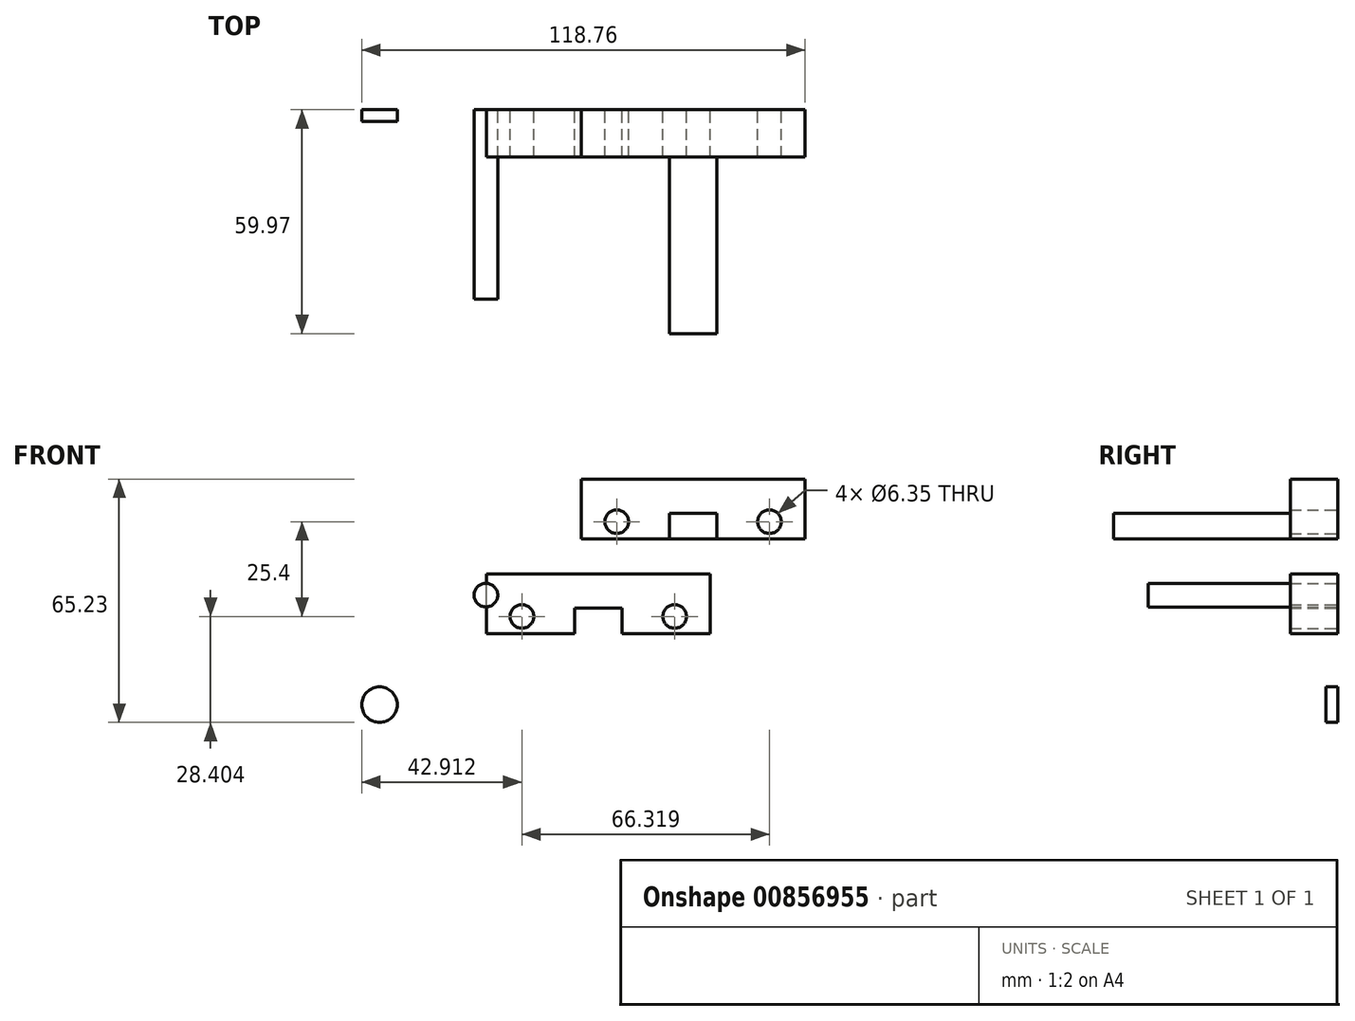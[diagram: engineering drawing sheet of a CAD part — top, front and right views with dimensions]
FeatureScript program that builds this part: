
annotation { "Feature Type Name" : "Feature", "Feature Type Description" : "" }
export const myFeature = defineFeature(function(context is Context, id is Id, definition is map)
    precondition{}
    {
        {
            var Q0;
            Q0=qCreatedBy(makeId("Front.planeOp"),FACE);
            var sketch = newSketch(context, id + "F0", { "sketchPlane" : qUnion([Q0])});
            skLineSegment(sketch, "E0", {"start": v(-17.85, 21.68) * mm, "end": v(42.12, 21.68) * mm});
            skLineSegment(sketch, "E1", {"start": v(42.12, 21.68) * mm, "end": v(42.12, 5.66) * mm});
            skLineSegment(sketch, "E2", {"start": v(-17.85, 5.66) * mm, "end": v(-17.85, 21.68) * mm});
            skLineSegment(sketch, "E3", {"start": v(-17.85, 5.66) * mm, "end": v(5.78, 5.66) * mm});
            skLineSegment(sketch, "E4", {"start": v(5.78, 5.66) * mm, "end": v(5.78, 12.52) * mm});
            skLineSegment(sketch, "E5", {"start": v(5.78, 12.52) * mm, "end": v(18.48, 12.52) * mm});
            skLineSegment(sketch, "E6", {"start": v(18.48, 12.52) * mm, "end": v(18.48, 5.66) * mm});
            skLineSegment(sketch, "E7", {"start": v(18.48, 5.66) * mm, "end": v(42.12, 5.66) * mm});
            skCircle(sketch, "E8", {"center": v(32.6, 10.25) * mm, "radius": 3.18 * mm});
            skCircle(sketch, "E9", {"center": v(-8.33, 10.25) * mm, "radius": 3.18 * mm});
            skSolve(sketch);
        }
        {
            var Q0;
            Q0=makeQuery(id+"F0.imprint","IMPRINT",FACE,{"disambiguationData":[TD([[makeQuery(id+"F0.imprint","IMPRINT",EDGE,{"derivedFrom":sQuery(id+"F0.wireOp",EDGE,"E0")}),-1.0]])]});
            extrude(context, id + "F1", {"entities" : qUnion([Q0]), "surfaceOperationType" : NewSurfaceOperationType.ADD, "depth" : 12.7 * mm, "offsetDistance" : 25.4 * mm});
        }
        {
            var Q0;
            Q0=makeQuery(id+"F1.opExtrude","SWEPT_BODY",BODY,{"disambiguationData":[OSD([sQuery(id+"F0.wireOp",EDGE,"E0"),sQuery(id+"F0.wireOp",EDGE,"E1"),sQuery(id+"F0.wireOp",EDGE,"E2"),sQuery(id+"F0.wireOp",EDGE,"E3"),sQuery(id+"F0.wireOp",EDGE,"E4"),sQuery(id+"F0.wireOp",EDGE,"E5"),sQuery(id+"F0.wireOp",EDGE,"E6"),sQuery(id+"F0.wireOp",EDGE,"E7")])]});
            transform(context, id + "F2", {"entities" : qUnion([Q0]), "transformType" : TransformType.TRANSLATION_3D, "dx" : 25.4 * mm, "dy" : 0 * mm, "dz" : 25.4 * mm, "makeCopy" : true});
        }
        {
            var Q0;
            Q0=makeQuery(id+"F2.opPattern","COPY",FACE,{"derivedFrom":makeQuery(id+"F1.opExtrude","CAP_FACE",FACE,{"disambiguationData":[OSD([sQuery(id+"F0.wireOp",EDGE,"E0"),sQuery(id+"F0.wireOp",EDGE,"E1"),sQuery(id+"F0.wireOp",EDGE,"E2"),sQuery(id+"F0.wireOp",EDGE,"E3"),sQuery(id+"F0.wireOp",EDGE,"E4"),sQuery(id+"F0.wireOp",EDGE,"E5"),sQuery(id+"F0.wireOp",EDGE,"E6"),sQuery(id+"F0.wireOp",EDGE,"E7")])],"isStart":true}),"instanceName":"1"});
            var sketch = newSketch(context, id + "F3", { "sketchPlane" : qUnion([Q0])});
            skLineSegment(sketch, "E10.bottom", {"start": v(-43.88, 31.06) * mm, "end": v(-31.18, 31.06) * mm});
            skLineSegment(sketch, "E10.top", {"start": v(-43.88, 37.92) * mm, "end": v(-31.18, 37.92) * mm});
            skLineSegment(sketch, "E10.left", {"start": v(-43.88, 31.06) * mm, "end": v(-43.88, 37.92) * mm});
            skLineSegment(sketch, "E10.right", {"start": v(-31.18, 31.06) * mm, "end": v(-31.18, 37.92) * mm});
            skCircle(sketch, "E11", {"center": v(-58, 35.65) * mm, "radius": 3.18 * mm});
            skCircle(sketch, "E12", {"center": v(-17.07, 35.65) * mm, "radius": 3.18 * mm});
            skSolve(sketch);
        }
        {
            var Q0;
            Q0=makeQuery(id+"F3.imprint","IMPRINT",FACE,{"disambiguationData":[TD([[makeQuery(id+"F3.imprint","IMPRINT",EDGE,{"derivedFrom":sQuery(id+"F3.wireOp",EDGE,"E10.bottom")}),1.0]])]});
            extrude(context, id + "F4", {"entities" : qUnion([Q0]), "operationType" : NewBodyOperationType.ADD, "depth" : -59.97 * mm, "offsetDistance" : 25.4 * mm});
        }
        {
            var Q0;
            Q0=sQuery(id+"F3.wireOp",VERTEX,"E11.center");
            var Q1;
            Q1=sQuery(id+"F3.wireOp",VERTEX,"E12.center");
            var Q2;
            Q2=makeQuery(id+"F2.opPattern","COPY",BODY,{"derivedFrom":makeQuery(id+"F1.opExtrude","SWEPT_BODY",BODY,{"disambiguationData":[OSD([sQuery(id+"F0.wireOp",EDGE,"E0"),sQuery(id+"F0.wireOp",EDGE,"E1"),sQuery(id+"F0.wireOp",EDGE,"E2"),sQuery(id+"F0.wireOp",EDGE,"E3"),sQuery(id+"F0.wireOp",EDGE,"E4"),sQuery(id+"F0.wireOp",EDGE,"E5"),sQuery(id+"F0.wireOp",EDGE,"E6"),sQuery(id+"F0.wireOp",EDGE,"E7")])]}),"instanceName":"1"});
            hole(context, id + "F5", {"style" : HoleStyle.SIMPLE, "endStyle" : HoleEndStyle.THROUGH, "holeDiameter" : 6.35 * mm, "majorDiameter" : 6.35 * mm, "isTappedThrough" : true, "tappedDepth" : 12.7 * mm, "tapClearance" : 3, "locations" : qUnion([Q0, Q1]), "scope" : qUnion([Q2])});
        }
        {
            var Q0;
            Q0=qCreatedBy(makeId("Front.planeOp"),FACE);
            var sketch = newSketch(context, id + "F6", { "sketchPlane" : qUnion([Q0])});
            skCircle(sketch, "E13", {"center": v(-17.99, 15.97) * mm, "radius": 3.17 * mm});
            skSolve(sketch);
        }
        {
            var Q0;
            Q0 = qSketchRegion(id + "F6", true);
            extrude(context, id + "F7", {"entities" : qUnion([Q0]), "depth" : 50.8 * mm, "offsetDistance" : 25.4 * mm});
        }
        {
            var Q0;
            Q0=qCreatedBy(makeId("Front.planeOp"),FACE);
            var sketch = newSketch(context, id + "F8", { "sketchPlane" : qUnion([Q0])});
            skCircle(sketch, "E14", {"center": v(-46.48, -13.38) * mm, "radius": 4.76 * mm});
            skSolve(sketch);
        }
        {
            var Q0;
            Q0 = qSketchRegion(id + "F8", true);
            extrude(context, id + "F9", {"entities" : qUnion([Q0]), "depth" : 3.17 * mm, "offsetDistance" : 25.4 * mm});
        }
    });
